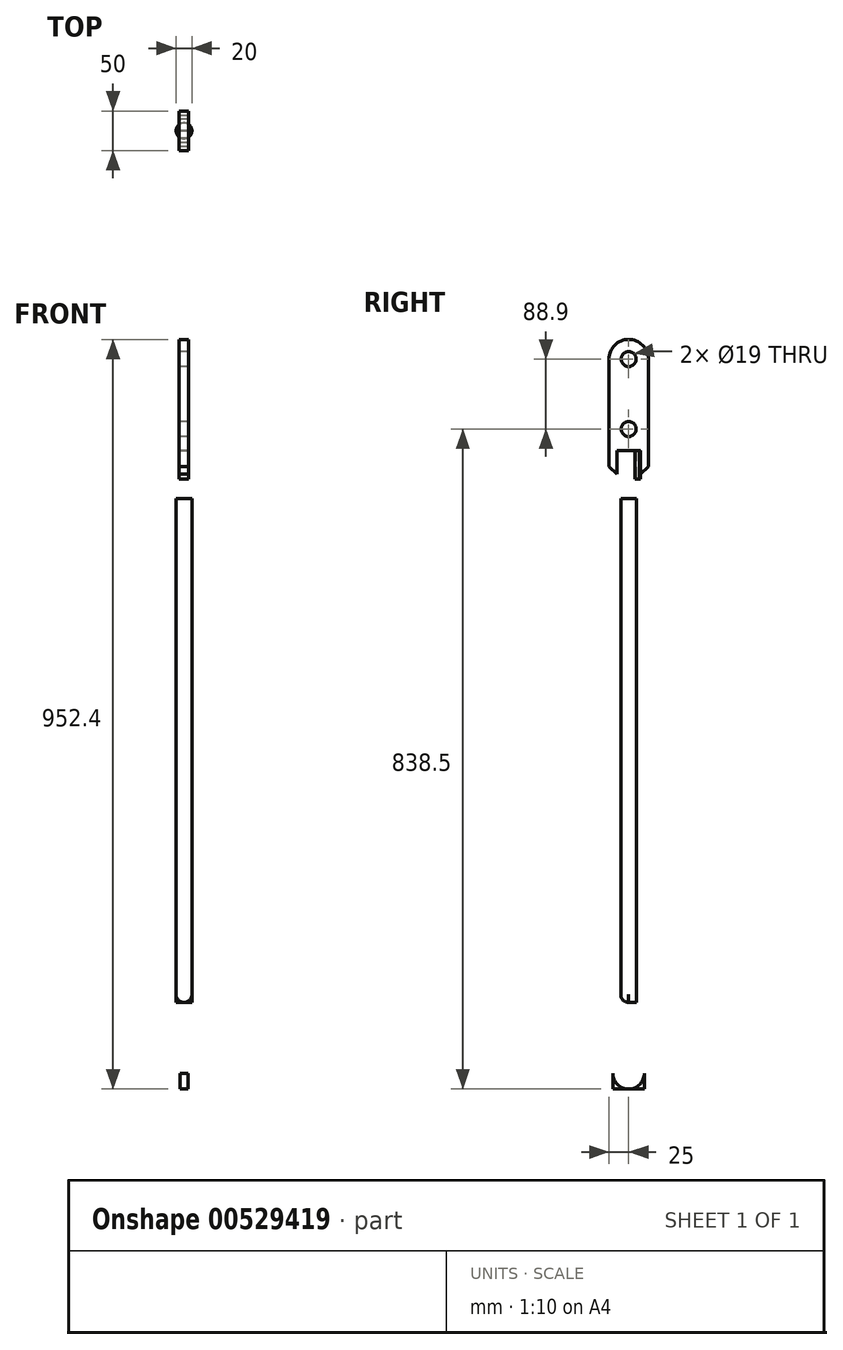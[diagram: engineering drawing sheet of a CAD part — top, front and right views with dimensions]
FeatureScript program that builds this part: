
annotation { "Feature Type Name" : "Feature", "Feature Type Description" : "" }
export const myFeature = defineFeature(function(context is Context, id is Id, definition is map)
    precondition{}
    {
        {
            var Q0;
            Q0=qCreatedBy(makeId("Top.planeOp"),FACE);
            var sketch = newSketch(context, id + "F0", { "sketchPlane" : qUnion([Q0])});
            skLineSegment(sketch, "E0.bottom", {"start": v(-6, 25) * mm, "end": v(6, 25) * mm});
            skLineSegment(sketch, "E0.top", {"start": v(-6, -25) * mm, "end": v(6, -25) * mm});
            skLineSegment(sketch, "E0.left", {"start": v(-6, 25) * mm, "end": v(-6, -25) * mm});
            skLineSegment(sketch, "E0.right", {"start": v(6, 25) * mm, "end": v(6, -25) * mm});
            skPoint(sketch, "E0.middle", {"position": v(0, 0) * mm});
            skSolve(sketch);
        }
        {
            var Q0;
            Q0=makeQuery(id+"F0.imprint","IMPRINT",FACE,{"disambiguationData":[TD([[makeQuery(id+"F0.imprint","IMPRINT",EDGE,{"derivedFrom":sQuery(id+"F0.wireOp",EDGE,"E0.bottom")}),-1.0]])]});
            extrude(context, id + "F1", {"entities" : qUnion([Q0]), "depth" : 171.4 * mm, "offsetDistance" : 25 * mm});
        }
        {
            var Q0;
            Q0=makeQuery(id+"F1.opExtrude","SWEPT_FACE",FACE,{"disambiguationData":[OSD([sQuery(id+"F0.wireOp",EDGE,"E0.left")])]});
            var sketch = newSketch(context, id + "F2", { "sketchPlane" : qUnion([Q0])});
            skLineSegment(sketch, "E1", {"start": v(0, 0) * mm, "end": v(0, 171.4) * mm, "construction": true});
            skLineSegment(sketch, "E2", {"start": v(-25, 85.7) * mm, "end": v(25, 85.7) * mm, "construction": true});
            skLineSegment(sketch, "E3", {"start": v(-15, 30) * mm, "end": v(-25, 30) * mm, "construction": true});
            skLineSegment(sketch, "E4", {"start": v(-15, 30) * mm, "end": v(-15, 0) * mm});
            skLineSegment(sketch, "E5.MirrorCS", {"start": v(15, 30) * mm, "end": v(15, 0) * mm});
            skLineSegment(sketch, "E6.MirrorCS", {"start": v(15, 30) * mm, "end": v(25, 30) * mm, "construction": true});
            skLineSegment(sketch, "E7", {"start": v(-15, 30) * mm, "end": v(15, 30) * mm});
            skLineSegment(sketch, "E8", {"start": v(-15, 0) * mm, "end": v(-25, 10) * mm});
            skLineSegment(sketch, "E9.MirrorCS", {"start": v(15, 0) * mm, "end": v(25, 10) * mm});
            skCircle(sketch, "E10", {"center": v(0, 57.5) * mm, "radius": 9.5 * mm});
            skCircle(sketch, "E11", {"center": v(0, 146.4) * mm, "radius": 9.5 * mm});
            skLineSegment(sketch, "E12", {"start": v(0, 146.4) * mm, "end": v(-25, 146.4) * mm, "construction": true});
            skArc(sketch, "E13", {"start": v(25, 146.4) * mm, "mid": v(0, 171.4) * mm, "end": v(-25, 146.4) * mm});
            skSolve(sketch);
        }
        {
            var Q0;
            {var subQ0=sQuery(id+"F2.wireOp",EDGE,"E8");Q0=makeQuery(id+"F2.imprint","IMPRINT",FACE,{"disambiguationData":[TD([[makeQuery(id+"F2.imprint","IMPRINT",EDGE,{"derivedFrom":subQ0}),1.0]])]});}
            var Q1;
            {var subQ0=sQuery(id+"F2.wireOp",EDGE,"E9.MirrorCS");Q1=makeQuery(id+"F2.imprint","IMPRINT",FACE,{"disambiguationData":[TD([[makeQuery(id+"F2.imprint","IMPRINT",EDGE,{"derivedFrom":subQ0}),-1.0]])]});}
            var Q2;
            {var subQ0=sQuery(id+"F2.wireOp",EDGE,"E13");var subQ1=sQuery(id+"F0.wireOp",EDGE,"E0.left");var subQ4=makeQuery(id+"F1.opExtrude","CAP_EDGE",EDGE,{"disambiguationData":[OSD([subQ1])],"isStart":false});var subQ5=makeQuery(id+"F2.imprint","INTERSECT",VERTEX,{"derivedFrom":[subQ4,subQ0]});Q2=makeQuery(id+"F2.imprint","IMPRINT",FACE,{"disambiguationData":[TD([[makeQuery(id+"F2.imprint","IMPRINT",EDGE,{"disambiguationData":[TD([[subQ5,-1.0]])],"derivedFrom":subQ0}),-1.0]])]});}
            var Q3;
            {var subQ0=sQuery(id+"F2.wireOp",EDGE,"E13");var subQ1=sQuery(id+"F0.wireOp",EDGE,"E0.left");var subQ4=makeQuery(id+"F1.opExtrude","CAP_EDGE",EDGE,{"disambiguationData":[OSD([subQ1])],"isStart":false});var subQ5=makeQuery(id+"F2.imprint","INTERSECT",VERTEX,{"derivedFrom":[subQ4,subQ0]});Q3=makeQuery(id+"F2.imprint","IMPRINT",FACE,{"disambiguationData":[TD([[makeQuery(id+"F2.imprint","IMPRINT",EDGE,{"disambiguationData":[TD([[subQ5,1.0]])],"derivedFrom":subQ0}),-1.0]])]});}
            var Q4;
            Q4=makeQuery(id+"F2.imprint","IMPRINT",FACE,{"disambiguationData":[TD([[makeQuery(id+"F2.imprint","IMPRINT",EDGE,{"derivedFrom":sQuery(id+"F2.wireOp",EDGE,"E11")}),1.0]])]});
            var Q5;
            Q5=makeQuery(id+"F2.imprint","IMPRINT",FACE,{"disambiguationData":[TD([[makeQuery(id+"F2.imprint","IMPRINT",EDGE,{"derivedFrom":sQuery(id+"F2.wireOp",EDGE,"E10")}),1.0]])]});
            var Q6;
            {var subQ0=sQuery(id+"F2.wireOp",EDGE,"E4");Q6=makeQuery(id+"F2.imprint","IMPRINT",FACE,{"disambiguationData":[TD([[makeQuery(id+"F2.imprint","IMPRINT",EDGE,{"derivedFrom":subQ0}),1.0]])]});}
            extrude(context, id + "F3", {"entities" : qUnion([Q0, Q1, Q2, Q3, Q4, Q5, Q6]), "operationType" : NewBodyOperationType.REMOVE, "oppositeDirection" : true, "depth" : 13 * mm, "offsetDistance" : 25 * mm});
        }
        {
            var Q0;
            Q0=makeQuery(id+"F3.boolean.opBoolean","COPY",FACE,{"derivedFrom":makeQuery(id+"F3.opExtrude","SWEPT_FACE",FACE,{"disambiguationData":[OSD([sQuery(id+"F2.wireOp",EDGE,"E7")])]})});
            var sketch = newSketch(context, id + "F4", { "sketchPlane" : qUnion([Q0])});
            skCircle(sketch, "E14", {"center": v(0, 0) * mm, "radius": 10 * mm});
            skCircle(sketch, "E15", {"center": v(0, 0) * mm, "radius": 15 * mm});
            skSolve(sketch);
        }
        {
            var Q0;
            {var subQ0=sQuery(id+"F4.wireOp",EDGE,"E14");var subQ1=makeQuery(id+"F3.boolean.opBoolean","INTERSECT",EDGE,{"derivedFrom":[makeQuery(id+"F1.opExtrude","SWEPT_FACE",FACE,{"disambiguationData":[OSD([sQuery(id+"F0.wireOp",EDGE,"E0.right")])]}),makeQuery(id+"F3.opExtrude","SWEPT_FACE",FACE,{"disambiguationData":[OSD([sQuery(id+"F2.wireOp",EDGE,"E7")])]})]});var subQ2=makeQuery(id+"F4.imprint","INTERSECT",VERTEX,{"disambiguationData":[OD(0.0)],"derivedFrom":[subQ1,subQ0]});Q0=makeQuery(id+"F4.imprint","IMPRINT",FACE,{"disambiguationData":[TD([[makeQuery(id+"F4.imprint","IMPRINT",EDGE,{"disambiguationData":[TD([[subQ2,1.0]])],"derivedFrom":subQ0}),-1.0]])]});}
            var Q1;
            {var subQ0=sQuery(id+"F4.wireOp",EDGE,"E15");var subQ1=sQuery(id+"F2.wireOp",EDGE,"E7");var subQ2=makeQuery(id+"F3.boolean.opBoolean","COPY",EDGE,{"derivedFrom":makeQuery(id+"F3.opExtrude","CAP_EDGE",EDGE,{"disambiguationData":[OSD([subQ1])],"isStart":true})});var subQ3=makeQuery(id+"F4.imprint","INTERSECT",VERTEX,{"disambiguationData":[OD(1.0)],"derivedFrom":[subQ2,subQ0]});Q1=makeQuery(id+"F4.imprint","IMPRINT",FACE,{"disambiguationData":[TD([[makeQuery(id+"F4.imprint","IMPRINT",EDGE,{"disambiguationData":[TD([[subQ3,-1.0]])],"derivedFrom":subQ2}),-1.0]])]});}
            var Q2;
            {var subQ0=sQuery(id+"F4.wireOp",EDGE,"E14");var subQ1=makeQuery(id+"F3.boolean.opBoolean","COPY",EDGE,{"derivedFrom":makeQuery(id+"F3.opExtrude","CAP_EDGE",EDGE,{"disambiguationData":[OSD([sQuery(id+"F2.wireOp",EDGE,"E7")])],"isStart":true})});var subQ2=makeQuery(id+"F4.imprint","INTERSECT",VERTEX,{"disambiguationData":[OD(0.0)],"derivedFrom":[subQ1,subQ0]});Q2=makeQuery(id+"F4.imprint","IMPRINT",FACE,{"disambiguationData":[TD([[makeQuery(id+"F4.imprint","IMPRINT",EDGE,{"disambiguationData":[TD([[subQ2,-1.0]])],"derivedFrom":subQ0}),-1.0]])]});}
            var Q3;
            {var subQ0=sQuery(id+"F4.wireOp",EDGE,"E15");var subQ1=sQuery(id+"F2.wireOp",EDGE,"E7");var subQ2=makeQuery(id+"F3.boolean.opBoolean","COPY",EDGE,{"derivedFrom":makeQuery(id+"F3.opExtrude","CAP_EDGE",EDGE,{"disambiguationData":[OSD([subQ1])],"isStart":true})});var subQ3=makeQuery(id+"F4.imprint","INTERSECT",VERTEX,{"disambiguationData":[OD(0.0)],"derivedFrom":[subQ2,subQ0]});Q3=makeQuery(id+"F4.imprint","IMPRINT",FACE,{"disambiguationData":[TD([[makeQuery(id+"F4.imprint","IMPRINT",EDGE,{"disambiguationData":[TD([[subQ3,1.0]])],"derivedFrom":subQ2}),-1.0]])]});}
            extrude(context, id + "F5", {"entities" : qUnion([Q0, Q1, Q2, Q3]), "depth" : 36 * mm, "offsetDistance" : 25 * mm});
        }
        {
            var Q0;
            Q0=makeQuery(id+"F5.opExtrude","CAP_FACE",FACE,{"disambiguationData":[OSD([sQuery(id+"F4.wireOp",EDGE,"E14"),sQuery(id+"F4.wireOp",EDGE,"E15")])],"isStart":false});
            cPlane(context, id + "F6", {"entities" : qUnion([Q0]), "cplaneType" : CPlaneType.OFFSET, "offset" : 25 * mm, "width" : 150 * mm, "height" : 150 * mm});
        }
        {
            var Q0;
            Q0=qCreatedBy(id+"F6.planeOp",FACE);
            var sketch = newSketch(context, id + "F7", { "sketchPlane" : qUnion([Q0])});
            skCircle(sketch, "E16", {"center": v(0, 0) * mm, "radius": 10 * mm});
            skSolve(sketch);
        }
        {
            var Q0;
            Q0=makeQuery(id+"F7.imprint","IMPRINT",FACE,{"disambiguationData":[TD([[makeQuery(id+"F7.imprint","IMPRINT",EDGE,{"derivedFrom":sQuery(id+"F7.wireOp",EDGE,"E16")}),1.0]])]});
            extrude(context, id + "F8", {"entities" : qUnion([Q0]), "depth" : 640 * mm, "offsetDistance" : 25 * mm});
        }
        {
            var Q0;
            Q0=makeQuery(id+"F8.opExtrude","CAP_FACE",FACE,{"disambiguationData":[OSD([sQuery(id+"F7.wireOp",EDGE,"E16")])],"isStart":false});
            cPlane(context, id + "F9", {"entities" : qUnion([Q0]), "cplaneType" : CPlaneType.OFFSET, "offset" : 25 * mm, "width" : 150 * mm, "height" : 150 * mm});
        }
        {
            var Q0;
            Q0=qCreatedBy(id+"F9.planeOp",FACE);
            var sketch = newSketch(context, id + "F10", { "sketchPlane" : qUnion([Q0])});
            skLineSegment(sketch, "E17.bottom", {"start": v(5, 20) * mm, "end": v(-5, 20) * mm});
            skLineSegment(sketch, "E17.top", {"start": v(5, -20) * mm, "end": v(-5, -20) * mm});
            skLineSegment(sketch, "E17.left", {"start": v(5, 20) * mm, "end": v(5, -20) * mm});
            skLineSegment(sketch, "E17.right", {"start": v(-5, 20) * mm, "end": v(-5, -20) * mm});
            skPoint(sketch, "E17.middle", {"position": v(0, 0) * mm});
            skSolve(sketch);
        }
        {
            var Q0;
            Q0=makeQuery(id+"F10.imprint","IMPRINT",FACE,{"disambiguationData":[TD([[makeQuery(id+"F10.imprint","IMPRINT",EDGE,{"derivedFrom":sQuery(id+"F10.wireOp",EDGE,"E17.bottom")}),1.0]])]});
            extrude(context, id + "F11", {"entities" : qUnion([Q0]), "depth" : 85 * mm, "offsetDistance" : 25 * mm});
        }
        {
            var Q0;
            Q0=makeQuery(id+"F11.opExtrude","SWEPT_FACE",FACE,{"disambiguationData":[OSD([sQuery(id+"F10.wireOp",EDGE,"E17.left")])]});
            var sketch = newSketch(context, id + "F12", { "sketchPlane" : qUnion([Q0])});
            skLineSegment(sketch, "E18", {"start": v(0, -696) * mm, "end": v(0, -781) * mm, "construction": true});
            skLineSegment(sketch, "E19", {"start": v(20, -738.5) * mm, "end": v(-20, -738.5) * mm, "construction": true});
            skLineSegment(sketch, "E20", {"start": v(10, -722.23) * mm, "end": v(10, -726.75) * mm, "construction": true});
            skLineSegment(sketch, "E21", {"start": v(10, -726.75) * mm, "end": v(10, -696) * mm});
            skLineSegment(sketch, "E22", {"start": v(10, -726.75) * mm, "end": v(0, -726.75) * mm, "construction": true});
            skLineSegment(sketch, "E23.MirrorCS", {"start": v(-10, -726.75) * mm, "end": v(0, -726.75) * mm, "construction": true});
            skLineSegment(sketch, "E24.MirrorCS", {"start": v(-10, -722.23) * mm, "end": v(-10, -726.75) * mm, "construction": true});
            skLineSegment(sketch, "E25.MirrorCS", {"start": v(-10, -726.75) * mm, "end": v(-10, -696) * mm});
            skLineSegment(sketch, "E26", {"start": v(10, -696) * mm, "end": v(20, -713.32) * mm});
            skPoint(sketch, "E27", {"position": v(0, -736.75) * mm});
            skArc(sketch, "E28", {"start": v(-10, -726.75) * mm, "mid": v(0, -736.75) * mm, "end": v(10, -726.75) * mm});
            skLineSegment(sketch, "E29.MirrorCS", {"start": v(-10, -696) * mm, "end": v(-20, -713.32) * mm});
            skCircle(sketch, "E30", {"center": v(0, -761) * mm, "radius": 9.5 * mm});
            skArc(sketch, "E31", {"start": v(20, -761) * mm, "mid": v(0, -781) * mm, "end": v(-20, -761) * mm});
            skSolve(sketch);
        }
        {
            var Q0;
            {var subQ0=sQuery(id+"F12.wireOp",EDGE,"E26");Q0=makeQuery(id+"F12.imprint","IMPRINT",FACE,{"disambiguationData":[TD([[makeQuery(id+"F12.imprint","IMPRINT",EDGE,{"derivedFrom":subQ0}),1.0]])]});}
            var Q1;
            {var subQ0=sQuery(id+"F12.wireOp",EDGE,"E31");var subQ1=sQuery(id+"F10.wireOp",EDGE,"E17.left");var subQ4=makeQuery(id+"F11.opExtrude","CAP_EDGE",EDGE,{"disambiguationData":[OSD([subQ1])],"isStart":false});var subQ5=makeQuery(id+"F12.imprint","INTERSECT",VERTEX,{"derivedFrom":[subQ4,subQ0]});Q1=makeQuery(id+"F12.imprint","IMPRINT",FACE,{"disambiguationData":[TD([[makeQuery(id+"F12.imprint","IMPRINT",EDGE,{"disambiguationData":[TD([[subQ5,1.0]])],"derivedFrom":subQ0}),1.0]])]});}
            var Q2;
            {var subQ0=sQuery(id+"F12.wireOp",EDGE,"E31");var subQ1=sQuery(id+"F10.wireOp",EDGE,"E17.left");var subQ4=makeQuery(id+"F11.opExtrude","CAP_EDGE",EDGE,{"disambiguationData":[OSD([subQ1])],"isStart":false});var subQ5=makeQuery(id+"F12.imprint","INTERSECT",VERTEX,{"derivedFrom":[subQ4,subQ0]});Q2=makeQuery(id+"F12.imprint","IMPRINT",FACE,{"disambiguationData":[TD([[makeQuery(id+"F12.imprint","IMPRINT",EDGE,{"disambiguationData":[TD([[subQ5,-1.0]])],"derivedFrom":subQ0}),1.0]])]});}
            var Q3;
            Q3=makeQuery(id+"F12.imprint","IMPRINT",FACE,{"disambiguationData":[TD([[makeQuery(id+"F12.imprint","IMPRINT",EDGE,{"derivedFrom":sQuery(id+"F12.wireOp",EDGE,"E30")}),1.0]])]});
            var Q4;
            {var subQ0=sQuery(id+"F12.wireOp",EDGE,"E29.MirrorCS");Q4=makeQuery(id+"F12.imprint","IMPRINT",FACE,{"disambiguationData":[TD([[makeQuery(id+"F12.imprint","IMPRINT",EDGE,{"derivedFrom":subQ0}),-1.0]])]});}
            var Q5;
            {var subQ0=sQuery(id+"F12.wireOp",EDGE,"E21");Q5=makeQuery(id+"F12.imprint","IMPRINT",FACE,{"disambiguationData":[TD([[makeQuery(id+"F12.imprint","IMPRINT",EDGE,{"derivedFrom":subQ0}),1.0]])]});}
            extrude(context, id + "F13", {"entities" : qUnion([Q0, Q1, Q2, Q3, Q4, Q5]), "operationType" : NewBodyOperationType.REMOVE, "oppositeDirection" : true, "depth" : 13 * mm, "offsetDistance" : 25 * mm});
        }
        {
            var Q0;
            Q0=qCreatedBy(makeId("Right.planeOp"),FACE);
            var sketch = newSketch(context, id + "F14", { "sketchPlane" : qUnion([Q0])});
            skLineSegment(sketch, "E32", {"start": v(10, -31) * mm, "end": v(10, -671) * mm});
            skLineSegment(sketch, "E33", {"start": v(-10, -671) * mm, "end": v(-10, -31) * mm});
            skLineSegment(sketch, "E34", {"start": v(10, -31) * mm, "end": v(-10, -31) * mm, "construction": true});
            skLineSegment(sketch, "E35", {"start": v(0, -31) * mm, "end": v(0, -671) * mm, "construction": true});
            skLineSegment(sketch, "E36.0", {"start": v(10, -671) * mm, "end": v(0, -671) * mm});
            skLineSegment(sketch, "E37", {"start": v(10, -671) * mm, "end": v(-10, -671) * mm});
            skLineSegment(sketch, "E38", {"start": v(0, -671) * mm, "end": v(-10, -671) * mm});
            skPoint(sketch, "E39", {"position": v(0, -661) * mm});
            skArc(sketch, "E40", {"start": v(10, -661) * mm, "mid": v(0, -671) * mm, "end": v(-10, -661) * mm});
            skLineSegment(sketch, "E41", {"start": v(10, -661) * mm, "end": v(10, -671) * mm});
            skLineSegment(sketch, "E42", {"start": v(-10, -661) * mm, "end": v(-10, -671) * mm});
            skSolve(sketch);
        }
        {
            var Q0;
            {var subQ0=sQuery(id+"F14.wireOp",EDGE,"E37");Q0=makeQuery(id+"F14.imprint","IMPRINT",FACE,{"disambiguationData":[TD([[makeQuery(id+"F14.imprint","IMPRINT",EDGE,{"derivedFrom":subQ0}),-1.0]])]});}
            var Q1;
            {var subQ0=sQuery(id+"F14.wireOp",EDGE,"E38");Q1=makeQuery(id+"F14.imprint","IMPRINT",FACE,{"disambiguationData":[TD([[makeQuery(id+"F14.imprint","IMPRINT",EDGE,{"derivedFrom":subQ0}),-1.0]])]});}
            var Q2;
            Q2=sQuery(id+"F14.wireOp",EDGE,"E35");
            revolve(context, id + "F15", {"operationType" : NewBodyOperationType.REMOVE, "entities" : qUnion([Q0, Q1]), "axis" : qUnion([Q2]), "revolveType" : RevolveType.SYMMETRIC, "oppositeDirection" : true, "angle" : 180 * degree});
        }
    });
